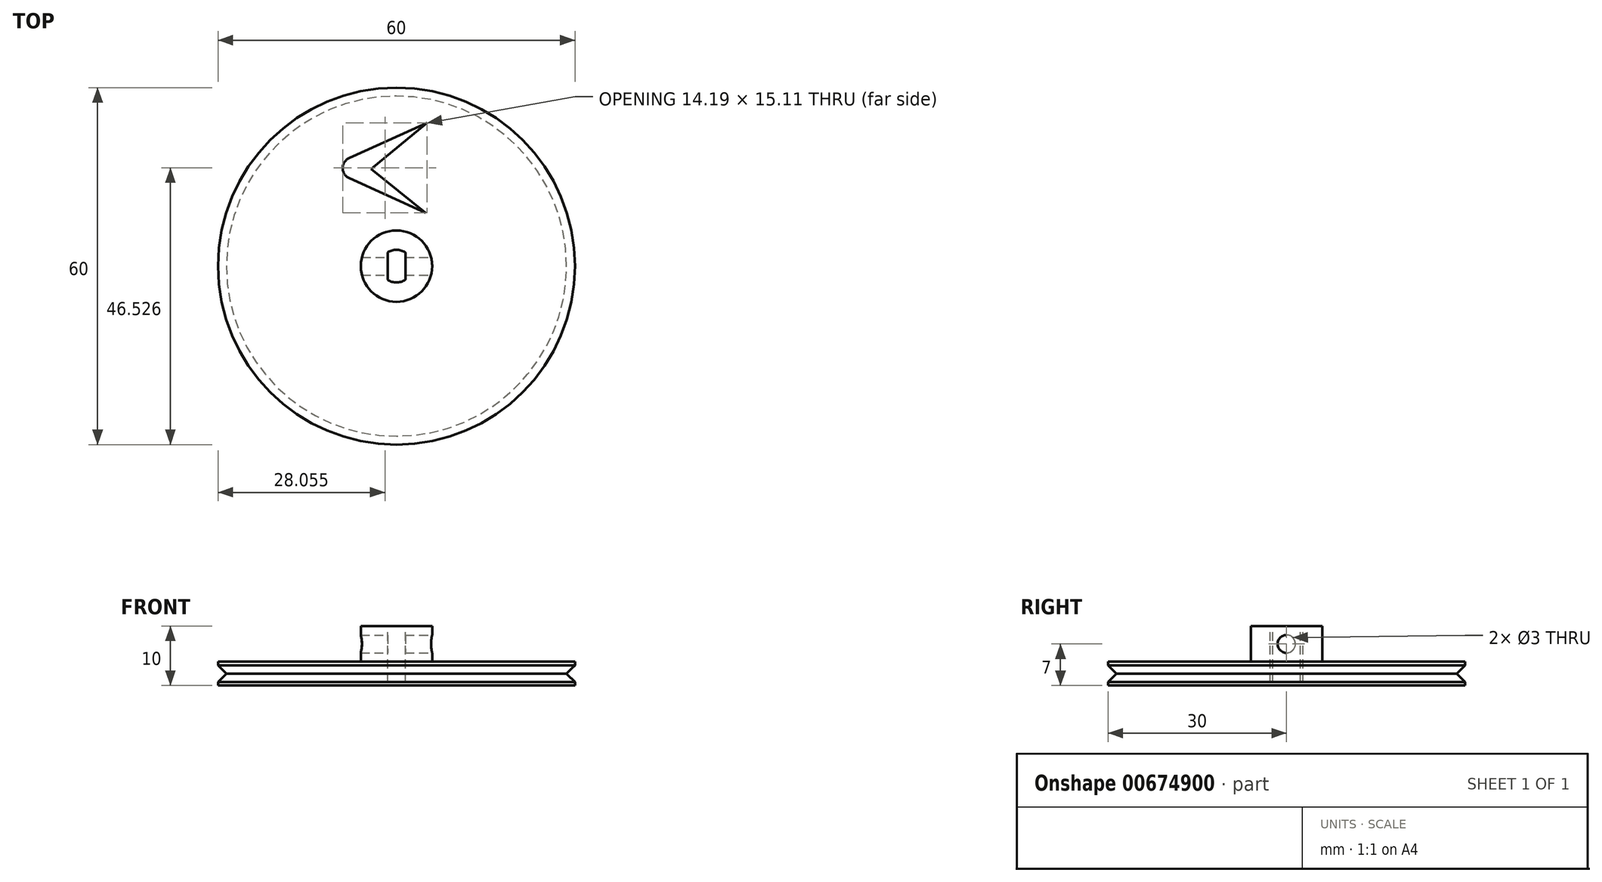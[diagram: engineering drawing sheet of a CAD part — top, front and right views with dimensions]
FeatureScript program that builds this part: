
annotation { "Feature Type Name" : "Feature", "Feature Type Description" : "" }
export const myFeature = defineFeature(function(context is Context, id is Id, definition is map)
    precondition{}
    {
        {
            var Q0;
            Q0=qCreatedBy(makeId("Top.planeOp"),FACE);
            var sketch = newSketch(context, id + "F0", { "sketchPlane" : qUnion([Q0])});
            skCircle(sketch, "E0", {"center": v(0, 0) * mm, "radius": 30 * mm});
            skCircle(sketch, "E1", {"center": v(0, 0) * mm, "radius": 6 * mm});
            skSolve(sketch);
        }
        {
            var Q0;
            Q0=qSketchRegion(id+"F0",true);
            var Q1;
            Q1=makeQuery(id+"F0.imprint","IMPRINT",FACE,{"disambiguationData":[TD([[makeQuery(id+"F0.imprint","IMPRINT",EDGE,{"derivedFrom":sQuery(id+"F0.wireOp",EDGE,"E1")}),1.0]])]});
            extrude(context, id + "F1", {"entities" : qUnion([Q0, Q1]), "oppositeDirection" : true, "depth" : 4 * mm, "offsetDistance" : 25 * mm});
        }
        {
            var Q0;
            Q0=makeQuery(id+"F0.imprint","IMPRINT",FACE,{"disambiguationData":[TD([[makeQuery(id+"F0.imprint","IMPRINT",EDGE,{"derivedFrom":sQuery(id+"F0.wireOp",EDGE,"E1")}),1.0]])]});
            extrude(context, id + "F2", {"entities" : qUnion([Q0]), "operationType" : NewBodyOperationType.ADD, "depth" : 6 * mm, "offsetDistance" : 25 * mm});
        }
        {
            var Q0;
            Q0=makeQuery(id+"F2.opExtrude","CAP_FACE",FACE,{"disambiguationData":[OSD([sQuery(id+"F0.wireOp",EDGE,"E1")])],"isStart":false});
            var sketch = newSketch(context, id + "F3", { "sketchPlane" : qUnion([Q0])});
            skLineSegment(sketch, "E2.bottom", {"start": v(-1.5, 2.3) * mm, "end": v(1.5, 2.3) * mm});
            skLineSegment(sketch, "E2.top", {"start": v(-1.5, -2.3) * mm, "end": v(1.5, -2.3) * mm});
            skLineSegment(sketch, "E2.left", {"start": v(-1.5, 2.3) * mm, "end": v(-1.5, -2.3) * mm});
            skLineSegment(sketch, "E2.right", {"start": v(1.5, 2.3) * mm, "end": v(1.5, -2.3) * mm});
            skPoint(sketch, "E2.middle", {"position": v(0, 0) * mm});
            skArc(sketch, "E3", {"start": v(1.5, 2.3) * mm, "mid": v(0, 2.75) * mm, "end": v(-1.5, 2.3) * mm});
            skArc(sketch, "E4", {"start": v(-1.5, -2.3) * mm, "mid": v(0, -2.75) * mm, "end": v(1.5, -2.3) * mm});
            skLineSegment(sketch, "E5", {"start": v(0, 2.75) * mm, "end": v(0, -2.75) * mm, "construction": true});
            skSolve(sketch);
        }
        {
            var Q0;
            Q0=makeQuery(id+"F3.imprint","IMPRINT",FACE,{"disambiguationData":[TD([[makeQuery(id+"F3.imprint","IMPRINT",EDGE,{"derivedFrom":sQuery(id+"F3.wireOp",EDGE,"E2.top")}),-1.0]])]});
            var Q1;
            Q1=makeQuery(id+"F3.imprint","IMPRINT",FACE,{"disambiguationData":[TD([[makeQuery(id+"F3.imprint","IMPRINT",EDGE,{"derivedFrom":sQuery(id+"F3.wireOp",EDGE,"E2.bottom")}),-1.0]])]});
            var Q2;
            Q2=makeQuery(id+"F3.imprint","IMPRINT",FACE,{"disambiguationData":[TD([[makeQuery(id+"F3.imprint","IMPRINT",EDGE,{"derivedFrom":sQuery(id+"F3.wireOp",EDGE,"E2.bottom")}),1.0]])]});
            extrude(context, id + "F4", {"entities" : qUnion([Q0, Q1, Q2]), "operationType" : NewBodyOperationType.REMOVE, "oppositeDirection" : true, "depth" : 9.4 * mm, "offsetDistance" : 25 * mm});
        }
        {
            var Q0;
            Q0=qCreatedBy(makeId("Front.planeOp"),FACE);
            var sketch = newSketch(context, id + "F5", { "sketchPlane" : qUnion([Q0])});
            skLineSegment(sketch, "E6.0", {"start": v(-30, 0) * mm, "end": v(30, 0) * mm});
            skLineSegment(sketch, "E7", {"start": v(-30, -4) * mm, "end": v(-30, 0) * mm});
            skLineSegment(sketch, "E8.0", {"start": v(-30, -4) * mm, "end": v(30, -4) * mm});
            skLineSegment(sketch, "E9", {"start": v(-30, 0) * mm, "end": v(-30, -0.59) * mm});
            skLineSegment(sketch, "E10", {"start": v(-30, -0.59) * mm, "end": v(-28.59, -2) * mm});
            skLineSegment(sketch, "E11", {"start": v(-28.59, -2) * mm, "end": v(-30, -3.41) * mm});
            skLineSegment(sketch, "E12", {"start": v(-30, -3.41) * mm, "end": v(-30, -4) * mm});
            skLineSegment(sketch, "E13", {"start": v(-30, -2) * mm, "end": v(-28.59, -2) * mm, "construction": true});
            skLineSegment(sketch, "E14", {"start": v(0, 8.8) * mm, "end": v(0, -9.1) * mm, "construction": true});
            skSolve(sketch);
        }
        {
            var Q0;
            Q0=qSketchRegion(id+"F5",true);
            var Q1;
            Q1=sQuery(id+"F5.wireOp",EDGE,"E14");
            revolve(context, id + "F6", {"operationType" : NewBodyOperationType.REMOVE, "entities" : qUnion([Q0]), "axis" : qUnion([Q1]), "revolveType" : RevolveType.FULL});
        }
        {
            var Q0;
            Q0=qCreatedBy(makeId("Right.planeOp"),FACE);
            cPlane(context, id + "F7", {"entities" : qUnion([Q0]), "cplaneType" : CPlaneType.OFFSET, "offset" : 25 * mm, "width" : 150 * mm, "height" : 150 * mm});
        }
        {
            var Q0;
            Q0=qCreatedBy(id+"F7.planeOp",FACE);
            var sketch = newSketch(context, id + "F8", { "sketchPlane" : qUnion([Q0])});
            skLineSegment(sketch, "E15", {"start": v(6, 6) * mm, "end": v(6, 0) * mm});
            skLineSegment(sketch, "E16", {"start": v(-6, 0) * mm, "end": v(-6, 6) * mm});
            skLineSegment(sketch, "E17.0", {"start": v(-6, 6) * mm, "end": v(6, 6) * mm});
            skLineSegment(sketch, "E18.0", {"start": v(-6, 0) * mm, "end": v(6, 0) * mm});
            skCircle(sketch, "E19", {"center": v(0, 3) * mm, "radius": 1.5 * mm});
            skPoint(sketch, "E19.centerSnap0", {"position": v(-6, 3) * mm});
            skSolve(sketch);
        }
        {
            var Q0;
            Q0=makeQuery(id+"F8.imprint","IMPRINT",FACE,{"disambiguationData":[TD([[makeQuery(id+"F8.imprint","IMPRINT",EDGE,{"derivedFrom":sQuery(id+"F8.wireOp",EDGE,"E19")}),1.0]])]});
            extrude(context, id + "F9", {"entities" : qUnion([Q0]), "operationType" : NewBodyOperationType.REMOVE, "oppositeDirection" : true, "depth" : 49.2 * mm, "offsetDistance" : 25 * mm});
        }
        {
            var Q0;
            Q0=makeQuery(id+"F0.imprint","IMPRINT",FACE,{"disambiguationData":[TD([[makeQuery(id+"F0.imprint","IMPRINT",EDGE,{"derivedFrom":sQuery(id+"F0.wireOp",EDGE,"E0")}),1.0]])]});
            var sketch = newSketch(context, id + "F10", { "sketchPlane" : qUnion([Q0])});
            skLineSegment(sketch, "E20", {"start": v(0, 38.3) * mm, "end": v(0, 0) * mm, "construction": true});
            skCircle(sketch, "E21", {"center": v(0, 0) * mm, "radius": 8 * mm, "construction": true});
            skCircle(sketch, "E22", {"center": v(0, 0) * mm, "radius": 28 * mm, "construction": true});
            skLineSegment(sketch, "E23", {"start": v(5.15, 24.08) * mm, "end": v(-7.95, 18.16) * mm});
            skLineSegment(sketch, "E24", {"start": v(4.9, 8.97) * mm, "end": v(-7.95, 14.79) * mm});
            skArc(sketch, "E25", {"start": v(-7.95, 18.16) * mm, "mid": v(-9.04, 16.47) * mm, "end": v(-7.95, 14.79) * mm});
            skLineSegment(sketch, "E26", {"start": v(5.15, 24.08) * mm, "end": v(-4.28, 16.32) * mm});
            skLineSegment(sketch, "E27", {"start": v(4.9, 8.97) * mm, "end": v(-4.28, 16.32) * mm});
            skSolve(sketch);
        }
        {
            var Q0;
            Q0=makeQuery(id+"F10.imprint","IMPRINT",FACE,{"disambiguationData":[TD([[makeQuery(id+"F10.imprint","IMPRINT",EDGE,{"derivedFrom":sQuery(id+"F10.wireOp",EDGE,"E23")}),1.0]])]});
            var Q1;
            Q1=makeQuery(id+"F1.opExtrude","CAP_FACE",FACE,{"disambiguationData":[OSD([sQuery(id+"F0.wireOp",EDGE,"E0")])],"isStart":false});
            extrude(context, id + "F11", {"entities" : qUnion([Q0]), "operationType" : NewBodyOperationType.REMOVE, "endBound" : BoundingType.UP_TO_SURFACE, "oppositeDirection" : true, "depth" : 25 * mm, "endBoundEntityFace" : qUnion([Q1]), "offsetDistance" : 25 * mm});
        }
    });
